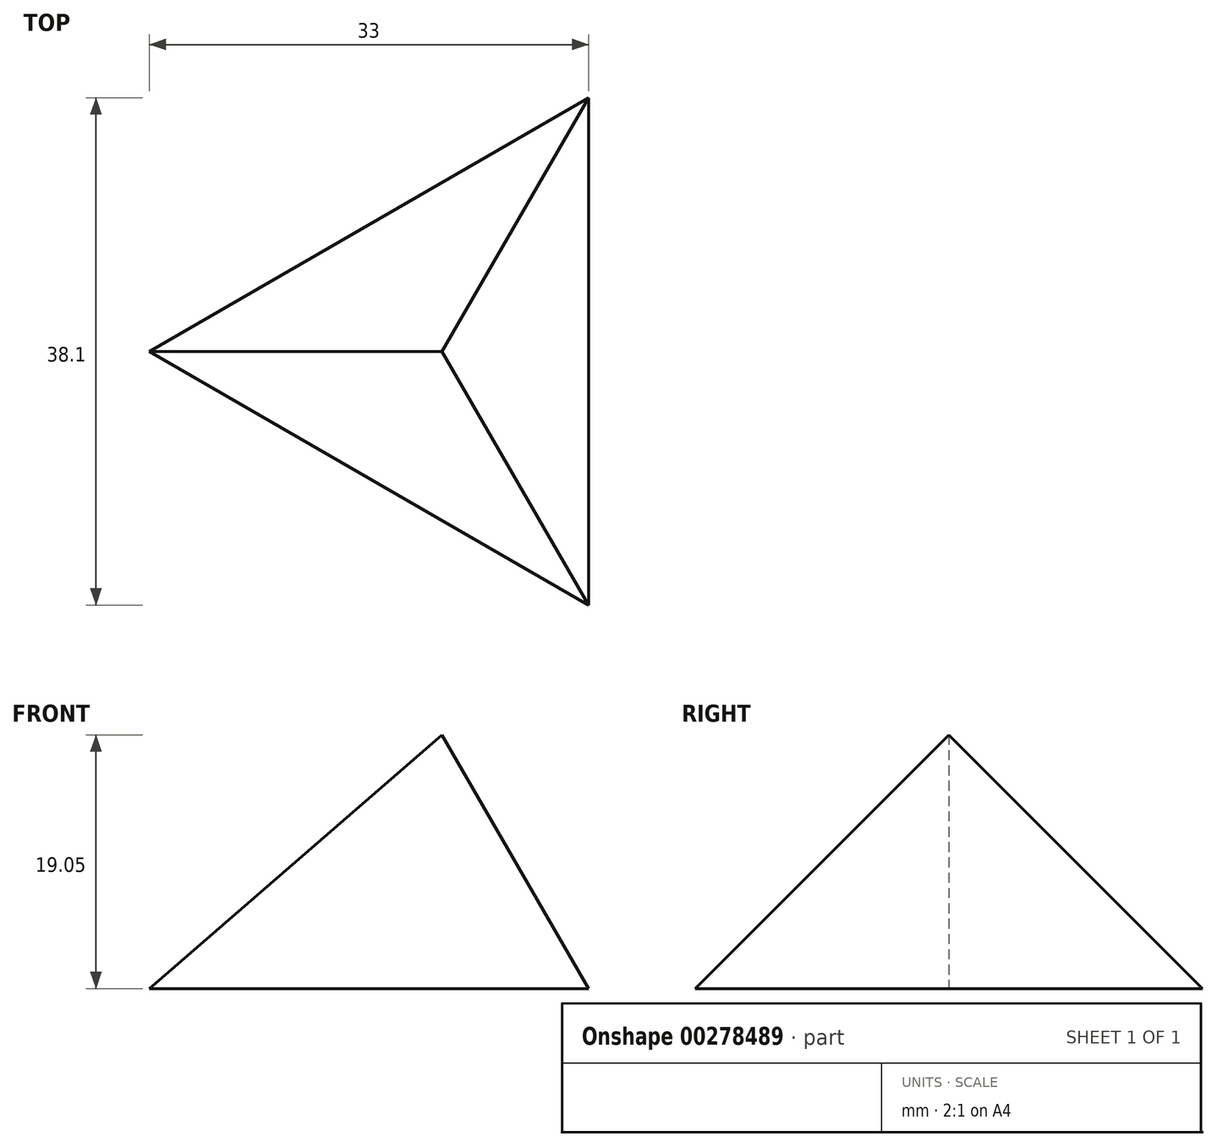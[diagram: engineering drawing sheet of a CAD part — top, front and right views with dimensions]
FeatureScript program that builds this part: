
annotation { "Feature Type Name" : "Feature", "Feature Type Description" : "" }
export const myFeature = defineFeature(function(context is Context, id is Id, definition is map)
    precondition{}
    {
        {
            var Q0;
            Q0=qCreatedBy(makeId("Top.planeOp"),FACE);
            var sketch = newSketch(context, id + "F0", { "sketchPlane" : qUnion([Q0])});
            skCircle(sketch, "E0.cCircle", {"center": v(0, 0) * mm, "radius": 11 * mm, "construction": true});
            skLineSegment(sketch, "E0.0", {"start": v(11, 19.05) * mm, "end": v(11, -19.05) * mm});
            skLineSegment(sketch, "E0.1", {"start": v(11, -19.05) * mm, "end": v(-22, 0) * mm});
            skLineSegment(sketch, "E0.2", {"start": v(-22, 0) * mm, "end": v(11, 19.05) * mm});
            skPoint(sketch, "E0.0.midPoint", {"position": v(11, 0) * mm});
            skSolve(sketch);
        }
        {
            var Q0;
            Q0 = qSketchRegion(id + "F0", true);
            extrude(context, id + "F1", {"entities" : qUnion([Q0]), "depth" : 19.05 * mm});
        }
        {
            var Q0;
            Q0=makeQuery(id+"F1.opExtrude","CAP_EDGE",EDGE,{"disambiguationData":[OSD([sQuery(id+"F0.wireOp",EDGE,"E0.1")])],"isStart":false});
            var Q1;
            Q1=makeQuery(id+"F1.opExtrude","CAP_EDGE",EDGE,{"disambiguationData":[OSD([sQuery(id+"F0.wireOp",EDGE,"E0.2")])],"isStart":false});
            var Q2;
            Q2=makeQuery(id+"F1.opExtrude","CAP_EDGE",EDGE,{"disambiguationData":[OSD([sQuery(id+"F0.wireOp",EDGE,"E0.0")])],"isStart":false});
            chamfer(context, id + "F2", {"entities" : qUnion([Q0, Q1, Q2]), "chamferType" : ChamferType.OFFSET_ANGLE, "width" : 19.05 * mm, "oppositeDirection" : false, "angle" : 30 * degree, "tangentPropagation" : true});
        }
    });
